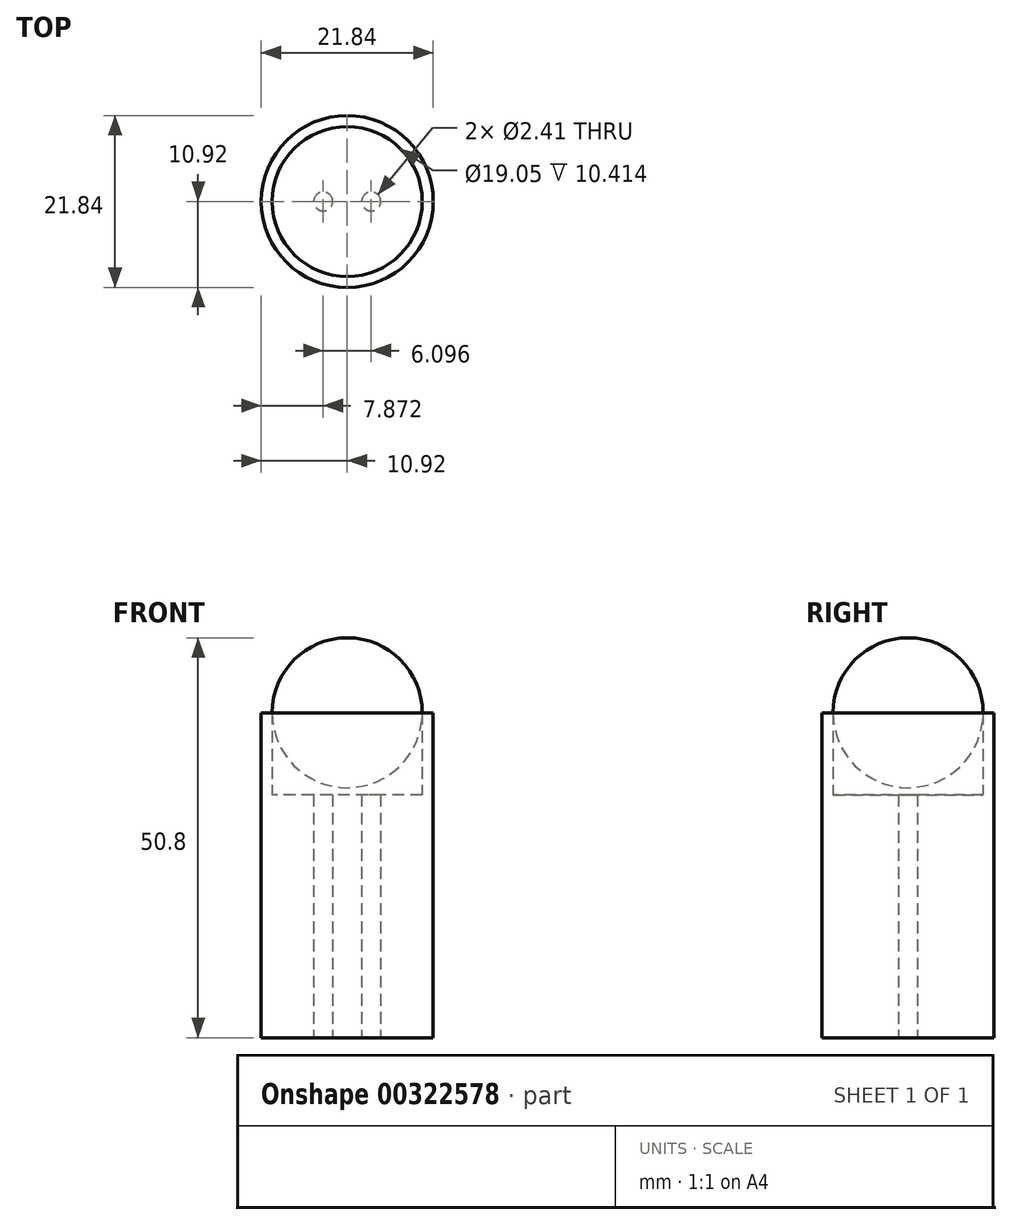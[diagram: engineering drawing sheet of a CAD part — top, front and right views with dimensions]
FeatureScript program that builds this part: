
annotation { "Feature Type Name" : "Feature", "Feature Type Description" : "" }
export const myFeature = defineFeature(function(context is Context, id is Id, definition is map)
    precondition{}
    {
        {
            var Q0;
            Q0=qCreatedBy(makeId("Top.planeOp"),FACE);
            var sketch = newSketch(context, id + "F0", { "sketchPlane" : qUnion([Q0])});
            skCircle(sketch, "E0", {"center": v(0, 0) * mm, "radius": 10.92 * mm});
            skCircle(sketch, "E1", {"center": v(0, 0) * mm, "radius": 9.53 * mm});
            skSolve(sketch);
        }
        {
            var Q0;
            Q0=makeQuery(id+"F0.imprint","IMPRINT",FACE,{"disambiguationData":[TD([[makeQuery(id+"F0.imprint","IMPRINT",EDGE,{"derivedFrom":sQuery(id+"F0.wireOp",EDGE,"E0")}),1.0]])]});
            extrude(context, id + "F1", {"entities" : qUnion([Q0]), "depth" : 13.6 * mm, "offsetDistance" : 25.4 * mm});
        }
        {
            var Q0;
            Q0=makeQuery(id+"F1.opExtrude","CAP_FACE",FACE,{"disambiguationData":[OSD([sQuery(id+"F0.wireOp",EDGE,"E0")])],"isStart":false});
            var sketch = newSketch(context, id + "F2", { "sketchPlane" : qUnion([Q0])});
            skLineSegment(sketch, "E2", {"start": v(-20.82, 0) * mm, "end": v(35.75, 0) * mm, "construction": true});
            skArc(sketch, "E3", {"start": v(-9.53, 0) * mm, "mid": v(0, -9.53) * mm, "end": v(9.53, 0) * mm});
            skLineSegment(sketch, "E4", {"start": v(-9.53, 0) * mm, "end": v(9.53, 0) * mm});
            skSolve(sketch);
        }
        {
            var Q0;
            Q0=makeQuery(id+"F2.imprint","IMPRINT",FACE,{"disambiguationData":[TD([[makeQuery(id+"F2.imprint","IMPRINT",EDGE,{"derivedFrom":sQuery(id+"F2.wireOp",EDGE,"E3")}),1.0]])]});
            var Q1;
            Q1=sQuery(id+"F2.wireOp",EDGE,"E2");
            revolve(context, id + "F3", {"entities" : qUnion([Q0]), "axis" : qUnion([Q1]), "revolveType" : RevolveType.FULL, "oppositeDirection" : true});
        }
        {
            var Q0;
            Q0=qCreatedBy(makeId("Top.planeOp"),FACE);
            var sketch = newSketch(context, id + "F4", { "sketchPlane" : qUnion([Q0])});
            skCircle(sketch, "E5", {"center": v(0, 0) * mm, "radius": 9.53 * mm});
            skCircle(sketch, "E6", {"center": v(3.05, 0) * mm, "radius": 1.2 * mm});
            skCircle(sketch, "E7.MirrorC", {"center": v(-3.05, 0) * mm, "radius": 1.2 * mm});
            skSolve(sketch);
        }
        {
            var Q0;
            Q0 = qSketchRegion(id + "F4", true);
            extrude(context, id + "F5", {"entities" : qUnion([Q0]), "operationType" : NewBodyOperationType.ADD, "depth" : 3.17 * mm, "offsetDistance" : 25.4 * mm});
        }
        {
            var Q0;
            Q0=makeQuery(id+"F5.boolean.opBoolean","MERGE",FACE,{"derivedFrom":[makeQuery(id+"F1.opExtrude","CAP_FACE",FACE,{"disambiguationData":[OSD([sQuery(id+"F0.wireOp",EDGE,"E0"),sQuery(id+"F0.wireOp",EDGE,"E1")])],"isStart":true}),makeQuery(id+"F5.opExtrude","CAP_FACE",FACE,{"disambiguationData":[OSD([sQuery(id+"F4.wireOp",EDGE,"E5"),sQuery(id+"F4.wireOp",EDGE,"E6"),sQuery(id+"F4.wireOp",EDGE,"E7.MirrorC")])],"isStart":true})]});
            extrude(context, id + "F6", {"entities" : qUnion([Q0]), "operationType" : NewBodyOperationType.ADD, "depth" : 27.7 * mm, "offsetDistance" : 25.4 * mm});
        }
    });
